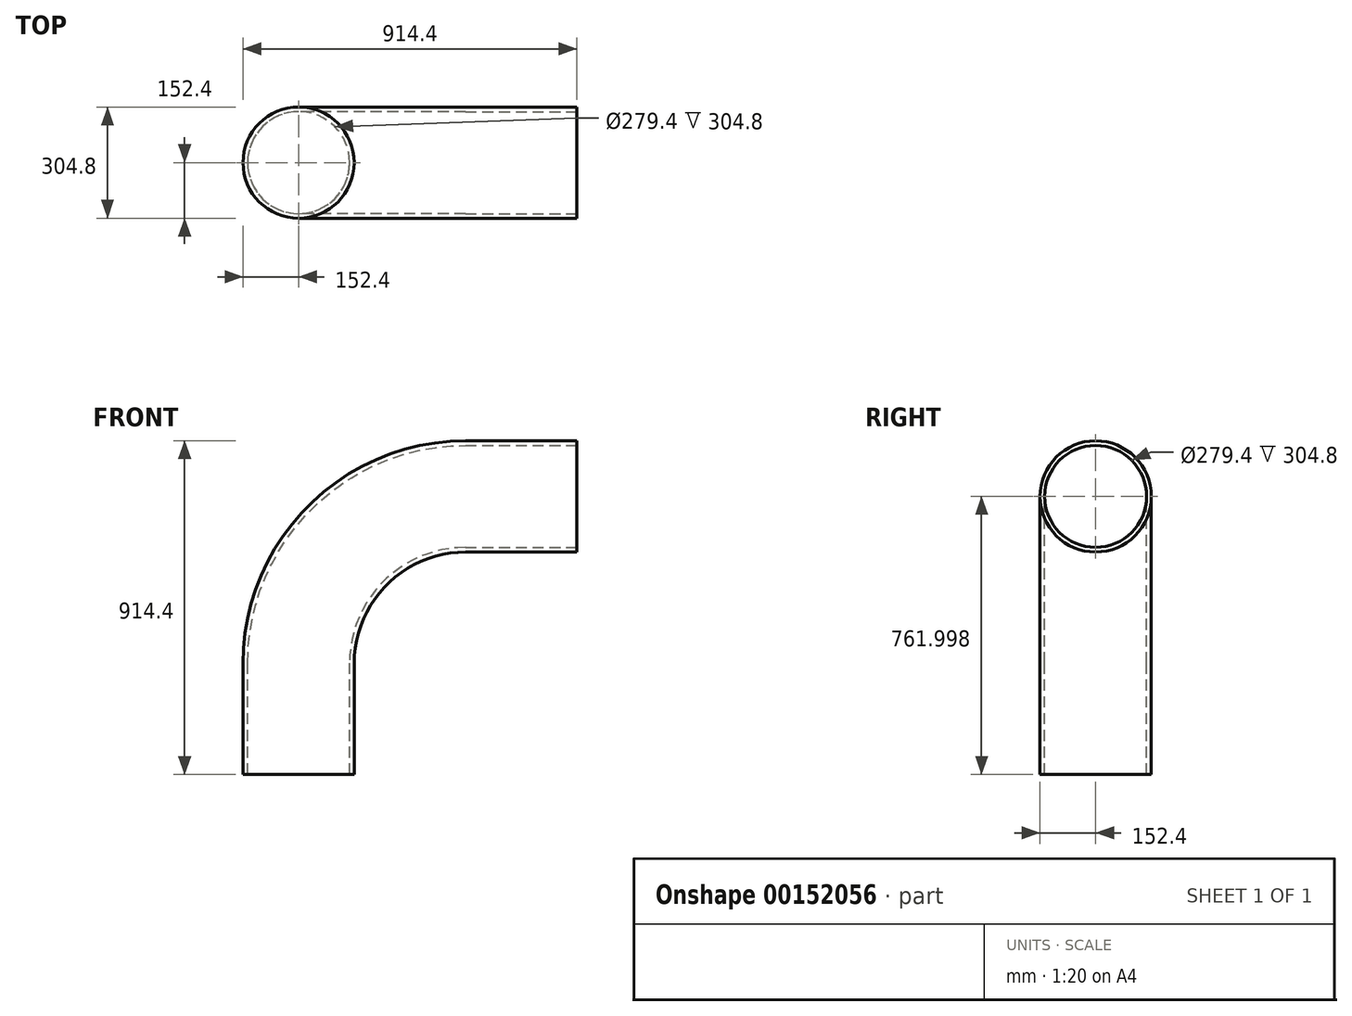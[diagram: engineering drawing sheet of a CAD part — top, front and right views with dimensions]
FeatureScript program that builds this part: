
annotation { "Feature Type Name" : "Feature", "Feature Type Description" : "" }
export const myFeature = defineFeature(function(context is Context, id is Id, definition is map)
    precondition{}
    {
        {
            var Q0;
            Q0=qCreatedBy(makeId("Front.planeOp"),FACE);
            var sketch = newSketch(context, id + "F0", { "sketchPlane" : qUnion([Q0])});
            skLineSegment(sketch, "E0.bottom", {"start": v(0, -74.64) * mm, "end": v(-304.8, -74.64) * mm});
            skLineSegment(sketch, "E0.left", {"start": v(0, -74.64) * mm, "end": v(0, 230.16) * mm});
            skLineSegment(sketch, "E0.right", {"start": v(-304.8, -74.64) * mm, "end": v(-304.8, 230.16) * mm});
            skLineSegment(sketch, "E1.bottom", {"start": v(304.8, 839.76) * mm, "end": v(609.6, 839.76) * mm});
            skLineSegment(sketch, "E1.top", {"start": v(304.8, 534.96) * mm, "end": v(609.6, 534.96) * mm});
            skLineSegment(sketch, "E1.right", {"start": v(609.6, 839.76) * mm, "end": v(609.6, 534.96) * mm});
            skArc(sketch, "E2", {"start": v(304.8, 534.96) * mm, "mid": v(89.27, 445.68) * mm, "end": v(0, 230.16) * mm});
            skArc(sketch, "E3", {"start": v(304.8, 839.76) * mm, "mid": v(-126.25, 661.21) * mm, "end": v(-304.8, 230.16) * mm});
            skPoint(sketch, "E4.orphan", {"position": v(0, 839.76) * mm});
            skPoint(sketch, "E5.orphan", {"position": v(0, 534.96) * mm});
            skSolve(sketch);
        }
        {
            var Q0;
            Q0 = qSketchRegion(id + "F0", true);
            extrude(context, id + "F1", {"entities" : qUnion([Q0]), "depth" : 304.8 * mm});
        }
        {
            var Q0;
            Q0=makeQuery(id+"F1.opExtrude","CAP_EDGE",EDGE,{"disambiguationData":[OSD([sQuery(id+"F0.wireOp",EDGE,"E3")])],"isStart":false});
            var Q1;
            Q1=makeQuery(id+"F1.opExtrude","CAP_EDGE",EDGE,{"disambiguationData":[OSD([sQuery(id+"F0.wireOp",EDGE,"E2")])],"isStart":false});
            var Q2;
            Q2=makeQuery(id+"F1.opExtrude","CAP_EDGE",EDGE,{"disambiguationData":[OSD([sQuery(id+"F0.wireOp",EDGE,"E3")])],"isStart":true});
            var Q3;
            Q3=makeQuery(id+"F1.opExtrude","CAP_EDGE",EDGE,{"disambiguationData":[OSD([sQuery(id+"F0.wireOp",EDGE,"E2")])],"isStart":true});
            fillet(context, id + "F2", {"entities" : qUnion([Q0, Q1, Q2, Q3]), "radius" : 152.4 * mm, "tangentPropagation" : true, "allowEdgeOverflow" : false});
        }
        {
            var Q0;
            Q0=makeQuery(id+"F1.opExtrude","SWEPT_FACE",FACE,{"disambiguationData":[OSD([sQuery(id+"F0.wireOp",EDGE,"E0.bottom")])]});
            var Q1;
            Q1=makeQuery(id+"F1.opExtrude","SWEPT_FACE",FACE,{"disambiguationData":[OSD([sQuery(id+"F0.wireOp",EDGE,"E1.right")])]});
            shell(context, id + "F3", {"entities" : qUnion([Q0, Q1]), "thickness" : 12.7 * mm});
        }
    });
